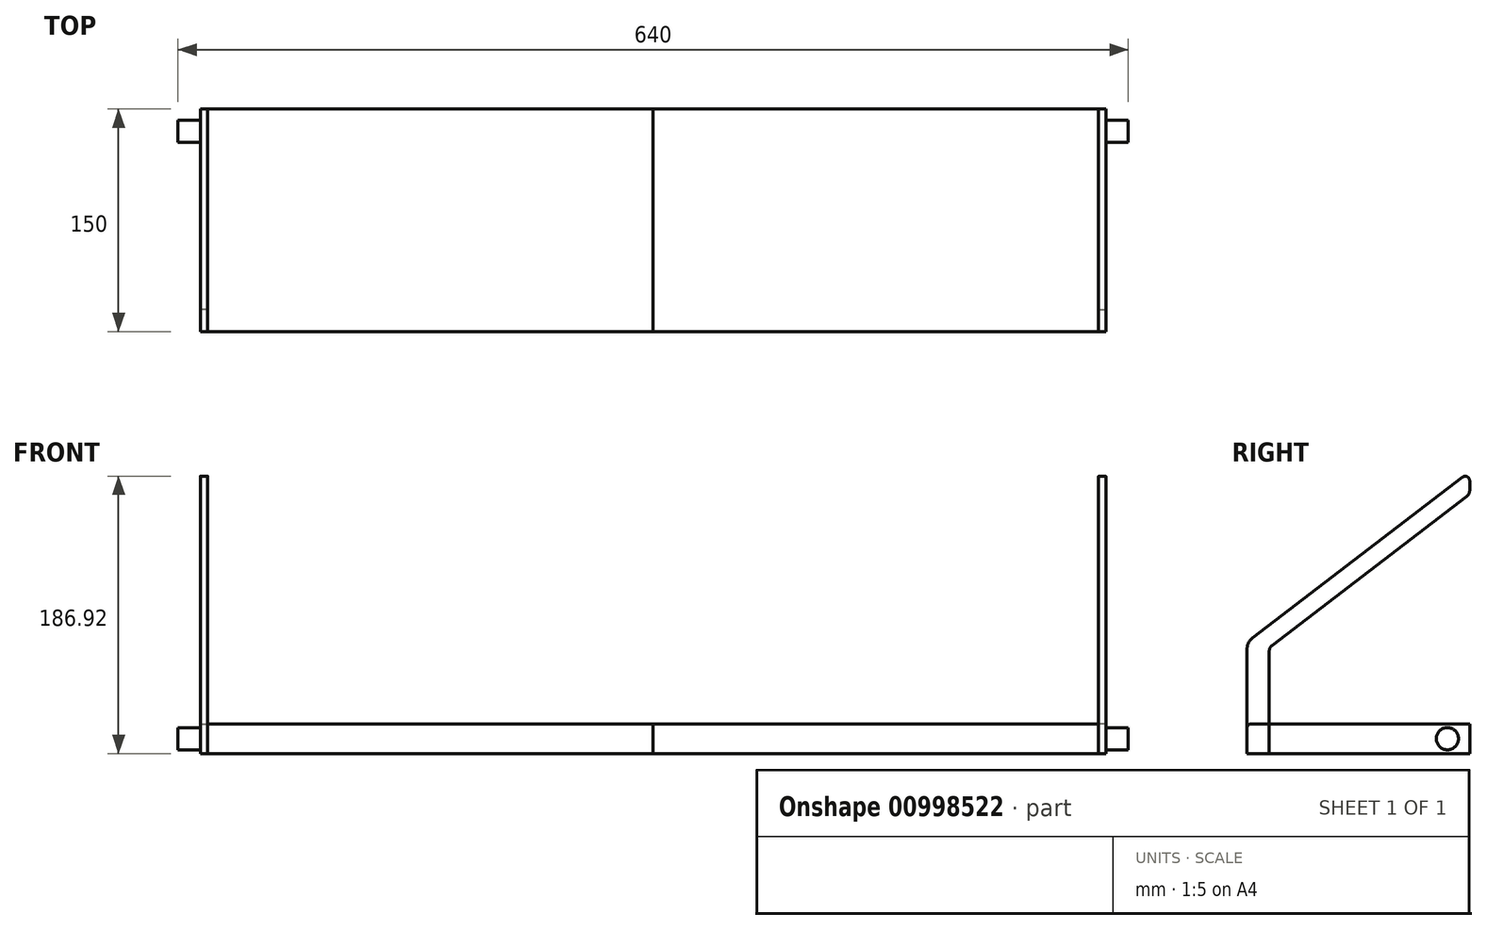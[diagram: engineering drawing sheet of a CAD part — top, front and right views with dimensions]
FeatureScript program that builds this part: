
annotation { "Feature Type Name" : "Feature", "Feature Type Description" : "" }
export const myFeature = defineFeature(function(context is Context, id is Id, definition is map)
    precondition{}
    {
        {
            var Q0;
            Q0=qCreatedBy(makeId("Right.planeOp"),FACE);
            var sketch = newSketch(context, id + "F0", { "sketchPlane" : qUnion([Q0])});
            skLineSegment(sketch, "E0.bottom", {"start": v(0, 0) * mm, "end": v(-150, 0) * mm});
            skLineSegment(sketch, "E0.top", {"start": v(0, 20) * mm, "end": v(-150, 20) * mm});
            skLineSegment(sketch, "E0.left", {"start": v(0, 0) * mm, "end": v(0, 20) * mm});
            skLineSegment(sketch, "E0.right", {"start": v(-150, 0) * mm, "end": v(-150, 20) * mm});
            skPoint(sketch, "E0.middle", {"position": v(-75, 10) * mm});
            skLineSegment(sketch, "E1", {"start": v(-150, 0) * mm, "end": v(-150, 70.07) * mm});
            skLineSegment(sketch, "E2", {"start": v(-146.08, 78) * mm, "end": v(-4.83, 186.3) * mm});
            skLineSegment(sketch, "E3", {"start": v(0, 183.92) * mm, "end": v(0, 177.35) * mm});
            skLineSegment(sketch, "E4", {"start": v(-1.96, 173.38) * mm, "end": v(-133.04, 72.88) * mm});
            skLineSegment(sketch, "E5", {"start": v(-135, 68.91) * mm, "end": v(-135, 0) * mm});
            skLineSegment(sketch, "E6", {"start": v(-135, 0) * mm, "end": v(-150, 0) * mm});
            skPoint(sketch, "E7.visualSharp", {"position": v(-150, 75) * mm});
            skArc(sketch, "E7.filletArc", {"start": v(-146.08, 78) * mm, "mid": v(-148.97, 74.5) * mm, "end": v(-150, 70.07) * mm});
            skPoint(sketch, "E8.visualSharp", {"position": v(-135, 71.38) * mm});
            skArc(sketch, "E8.filletArc", {"start": v(-133.04, 72.88) * mm, "mid": v(-134.48, 71.12) * mm, "end": v(-135, 68.91) * mm});
            skPoint(sketch, "E9.visualSharp", {"position": v(0, 174.88) * mm});
            skArc(sketch, "E9.filletArc", {"start": v(-1.96, 173.38) * mm, "mid": v(-0.52, 175.13) * mm, "end": v(0, 177.35) * mm});
            skPoint(sketch, "E10.visualSharp", {"position": v(0, 190) * mm});
            skArc(sketch, "E10.filletArc", {"start": v(0, 183.92) * mm, "mid": v(-1.67, 186.61) * mm, "end": v(-4.83, 186.3) * mm});
            skSolve(sketch);
        }
        {
            var Q0;
            {var subQ0=sQuery(id+"F0.wireOp",EDGE,"E0.bottom");Q0=makeQuery(id+"F0.imprint","IMPRINT",FACE,{"disambiguationData":[TD([[makeQuery(id+"F0.imprint","IMPRINT",EDGE,{"derivedFrom":subQ0}),-1.0]])]});}
            var Q1;
            {var subQ5=sQuery(id+"F0.wireOp",EDGE,"E6");Q1=makeQuery(id+"F0.imprint","IMPRINT",FACE,{"disambiguationData":[TD([[makeQuery(id+"F0.imprint","IMPRINT",EDGE,{"derivedFrom":subQ5}),-1.0]])]});}
            extrude(context, id + "F1", {"entities" : qUnion([Q0, Q1]), "depth" : 305 * mm, "offsetDistance" : 25 * mm});
        }
        {
            var Q0;
            Q0=makeQuery(id+"F1.opExtrude","CAP_FACE",FACE,{"disambiguationData":[OSD([sQuery(id+"F0.wireOp",EDGE,"E0.bottom"),sQuery(id+"F0.wireOp",EDGE,"E0.top"),sQuery(id+"F0.wireOp",EDGE,"E0.left"),sQuery(id+"F0.wireOp",EDGE,"E1"),sQuery(id+"F0.wireOp",EDGE,"E6")])],"isStart":false});
            var sketch = newSketch(context, id + "F2", { "sketchPlane" : qUnion([Q0])});
            skLineSegment(sketch, "E11.0.0", {"start": v(-4.83, 186.3) * mm, "end": v(-146.08, 78) * mm});
            skArc(sketch, "E11.0.1", {"start": v(-146.08, 78) * mm, "mid": v(-148.97, 74.5) * mm, "end": v(-150, 70.07) * mm});
            skLineSegment(sketch, "E11.0.2", {"start": v(-150, 70.07) * mm, "end": v(-150, 20) * mm});
            skLineSegment(sketch, "E11.0.3", {"start": v(-150, 20) * mm, "end": v(-135, 20) * mm});
            skLineSegment(sketch, "E11.0.4", {"start": v(-135, 20) * mm, "end": v(-135, 68.91) * mm});
            skArc(sketch, "E11.0.5", {"start": v(-135, 68.91) * mm, "mid": v(-134.48, 71.12) * mm, "end": v(-133.04, 72.88) * mm});
            skLineSegment(sketch, "E11.0.6", {"start": v(-133.04, 72.88) * mm, "end": v(-1.96, 173.38) * mm});
            skArc(sketch, "E11.0.7", {"start": v(-1.96, 173.38) * mm, "mid": v(-0.52, 175.13) * mm, "end": v(0, 177.35) * mm});
            skLineSegment(sketch, "E11.0.8", {"start": v(0, 177.35) * mm, "end": v(0, 183.92) * mm});
            skArc(sketch, "E11.0.9", {"start": v(0, 183.92) * mm, "mid": v(-1.67, 186.61) * mm, "end": v(-4.83, 186.3) * mm});
            skLineSegment(sketch, "E11.1.0", {"start": v(-150, 0) * mm, "end": v(-135, 0) * mm});
            skLineSegment(sketch, "E11.1.1", {"start": v(-135, 0) * mm, "end": v(-135, 20) * mm});
            skLineSegment(sketch, "E11.1.2", {"start": v(-135, 20) * mm, "end": v(-150, 20) * mm});
            skLineSegment(sketch, "E11.1.3", {"start": v(-150, 20) * mm, "end": v(-150, 0) * mm});
            skSolve(sketch);
        }
        {
            var Q0;
            Q0 = qSketchRegion(id + "F2", true);
            extrude(context, id + "F3", {"entities" : qUnion([Q0]), "oppositeDirection" : true, "depth" : 5 * mm, "offsetDistance" : 25 * mm});
        }
        {
            var Q0;
            Q0=makeQuery(id+"F1.opExtrude","SWEPT_EDGE",EDGE,{"disambiguationData":[OSD([sQuery(id+"F0.wireOp",EDGE,"E0.top"),sQuery(id+"F0.wireOp",EDGE,"E1")])]});
            var Q1;
            Q1=makeQuery(id+"F1.opExtrude","SWEPT_EDGE",EDGE,{"disambiguationData":[OSD([sQuery(id+"F0.wireOp",EDGE,"E1"),sQuery(id+"F0.wireOp",EDGE,"E6")])]});
            fillet(context, id + "F4", {"entities" : qUnion([Q0, Q1]), "radius" : 3 * mm, "tangentPropagation" : true, "allowEdgeOverflow" : false});
        }
        {
            var Q0;
            Q0=makeQuery(id+"F1.opExtrude","CAP_FACE",FACE,{"disambiguationData":[OSD([sQuery(id+"F0.wireOp",EDGE,"E0.bottom"),sQuery(id+"F0.wireOp",EDGE,"E0.top"),sQuery(id+"F0.wireOp",EDGE,"E0.left"),sQuery(id+"F0.wireOp",EDGE,"E1"),sQuery(id+"F0.wireOp",EDGE,"E6")])],"isStart":false});
            var sketch = newSketch(context, id + "F5", { "sketchPlane" : qUnion([Q0])});
            skLineSegment(sketch, "E12", {"start": v(-30, 20) * mm, "end": v(-30, 0) * mm, "construction": true});
            skLineSegment(sketch, "E13", {"start": v(-30, 10) * mm, "end": v(0, 10) * mm, "construction": true});
            skCircle(sketch, "E14", {"center": v(-15, 10) * mm, "radius": 7.5 * mm});
            skSolve(sketch);
        }
        {
            var Q0;
            Q0 = qSketchRegion(id + "F5", true);
            extrude(context, id + "F6", {"entities" : qUnion([Q0]), "operationType" : NewBodyOperationType.ADD, "depth" : 15 * mm, "offsetDistance" : 25 * mm});
        }
        {
            var Q0;
            Q0=makeQuery(id+"F1.opExtrude","SWEPT_BODY",BODY,{"disambiguationData":[OSD([sQuery(id+"F0.wireOp",EDGE,"E0.bottom"),sQuery(id+"F0.wireOp",EDGE,"E0.top"),sQuery(id+"F0.wireOp",EDGE,"E0.left"),sQuery(id+"F0.wireOp",EDGE,"E1"),sQuery(id+"F0.wireOp",EDGE,"E6")])]});
            var Q1;
            Q1=makeQuery(id+"F3.opExtrude","SWEPT_BODY",BODY,{"disambiguationData":[OSD([sQuery(id+"F2.wireOp",EDGE,"E11.0.0"),sQuery(id+"F2.wireOp",EDGE,"E11.0.1"),sQuery(id+"F2.wireOp",EDGE,"E11.0.2"),sQuery(id+"F2.wireOp",EDGE,"E11.0.4"),sQuery(id+"F2.wireOp",EDGE,"E11.0.5"),sQuery(id+"F2.wireOp",EDGE,"E11.0.6"),sQuery(id+"F2.wireOp",EDGE,"E11.0.7"),sQuery(id+"F2.wireOp",EDGE,"E11.0.8"),sQuery(id+"F2.wireOp",EDGE,"E11.0.9"),sQuery(id+"F2.wireOp",EDGE,"E11.1.0"),sQuery(id+"F2.wireOp",EDGE,"E11.1.1"),sQuery(id+"F2.wireOp",EDGE,"E11.1.3")])]});
            var Q2;
            Q2=qCreatedBy(makeId("Right.planeOp"),FACE);
            mirror(context, id + "F7", {"entities" : qUnion([Q0, Q1]), "mirrorPlane" : qUnion([Q2])});
        }
    });
